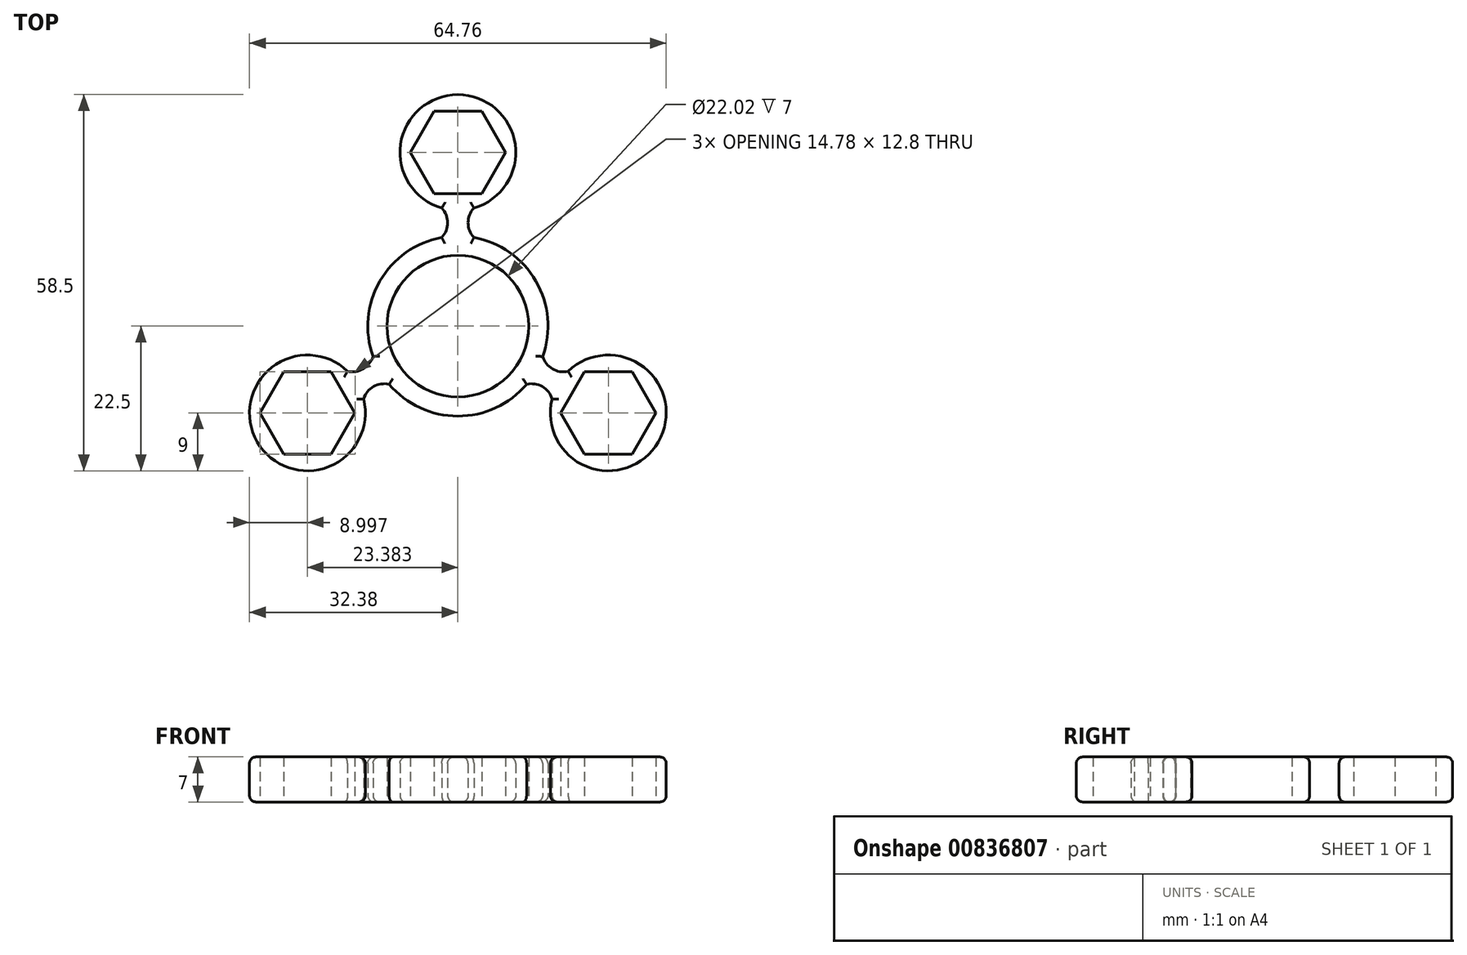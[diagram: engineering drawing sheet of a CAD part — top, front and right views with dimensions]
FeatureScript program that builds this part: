
annotation { "Feature Type Name" : "Feature", "Feature Type Description" : "" }
export const myFeature = defineFeature(function(context is Context, id is Id, definition is map)
    precondition{}
    {
        {
            var Q0;
            Q0=qCreatedBy(makeId("Top.planeOp"),FACE);
            var sketch = newSketch(context, id + "F0", { "sketchPlane" : qUnion([Q0])});
            skCircle(sketch, "E0", {"center": v(0, 0) * mm, "radius": 11.01 * mm});
            skArc(sketch, "E1", {"start": v(-2.5, 13.77) * mm, "mid": v(-12.12, 7) * mm, "end": v(-13.18, -4.72) * mm});
            skCircle(sketch, "E2.cCircle", {"center": v(0, 27) * mm, "radius": 6.4 * mm, "construction": true});
            skLineSegment(sketch, "E2.0", {"start": v(-7.4, 27) * mm, "end": v(-3.7, 33.4) * mm});
            skLineSegment(sketch, "E2.1", {"start": v(-3.7, 33.4) * mm, "end": v(3.7, 33.4) * mm});
            skLineSegment(sketch, "E2.2", {"start": v(3.7, 33.4) * mm, "end": v(7.4, 27) * mm});
            skLineSegment(sketch, "E2.3", {"start": v(7.4, 27) * mm, "end": v(3.7, 20.6) * mm});
            skLineSegment(sketch, "E2.4", {"start": v(3.7, 20.6) * mm, "end": v(-3.7, 20.6) * mm});
            skLineSegment(sketch, "E2.5", {"start": v(-3.7, 20.6) * mm, "end": v(-7.4, 27) * mm});
            skPoint(sketch, "E2.0.midPoint", {"position": v(-5.54, 30.2) * mm});
            skArc(sketch, "E3", {"start": v(2.5, 18.35) * mm, "mid": v(0, 36) * mm, "end": v(-2.5, 18.35) * mm});
            skArc(sketch, "E4", {"start": v(-2.5, 13.77) * mm, "mid": v(-1.59, 16.06) * mm, "end": v(-2.5, 18.35) * mm});
            skArc(sketch, "E5.MirrorCS", {"start": v(2.5, 13.77) * mm, "mid": v(1.59, 16.06) * mm, "end": v(2.5, 18.35) * mm});
            skArc(sketch, "E6.1.0", {"start": v(-17.15, -7.01) * mm, "mid": v(-31.18, -18) * mm, "end": v(-14.65, -11.34) * mm});
            skLineSegment(sketch, "E6.1.1", {"start": v(-27.08, -19.9) * mm, "end": v(-30.77, -13.5) * mm});
            skLineSegment(sketch, "E6.1.2", {"start": v(-19.69, -19.9) * mm, "end": v(-27.08, -19.9) * mm});
            skLineSegment(sketch, "E6.1.3", {"start": v(-16, -13.5) * mm, "end": v(-19.69, -19.9) * mm});
            skLineSegment(sketch, "E6.1.4", {"start": v(-19.69, -7.1) * mm, "end": v(-16, -13.5) * mm});
            skLineSegment(sketch, "E6.1.5", {"start": v(-27.08, -7.1) * mm, "end": v(-19.69, -7.1) * mm});
            skLineSegment(sketch, "E6.1.6", {"start": v(-30.77, -13.5) * mm, "end": v(-27.08, -7.1) * mm});
            skArc(sketch, "E6.1.7", {"start": v(-13.18, -4.72) * mm, "mid": v(-14.7, -6.66) * mm, "end": v(-17.15, -7.01) * mm});
            skArc(sketch, "E6.1.8", {"start": v(-10.68, -9.05) * mm, "mid": v(-13.12, -9.4) * mm, "end": v(-14.65, -11.34) * mm});
            skArc(sketch, "E6.2.0", {"start": v(14.65, -11.34) * mm, "mid": v(31.18, -18) * mm, "end": v(17.15, -7.01) * mm});
            skLineSegment(sketch, "E6.2.1", {"start": v(30.77, -13.5) * mm, "end": v(27.08, -19.9) * mm});
            skLineSegment(sketch, "E6.2.2", {"start": v(27.08, -7.1) * mm, "end": v(30.77, -13.5) * mm});
            skLineSegment(sketch, "E6.2.3", {"start": v(19.69, -7.1) * mm, "end": v(27.08, -7.1) * mm});
            skLineSegment(sketch, "E6.2.4", {"start": v(16, -13.5) * mm, "end": v(19.69, -7.1) * mm});
            skLineSegment(sketch, "E6.2.5", {"start": v(19.69, -19.9) * mm, "end": v(16, -13.5) * mm});
            skLineSegment(sketch, "E6.2.6", {"start": v(27.08, -19.9) * mm, "end": v(19.69, -19.9) * mm});
            skArc(sketch, "E6.2.7", {"start": v(10.68, -9.05) * mm, "mid": v(13.12, -9.4) * mm, "end": v(14.65, -11.34) * mm});
            skArc(sketch, "E6.2.8", {"start": v(13.18, -4.72) * mm, "mid": v(14.7, -6.66) * mm, "end": v(17.15, -7.01) * mm});
            skArc(sketch, "E7.trimOffspring", {"start": v(-10.68, -9.05) * mm, "mid": v(0, -14) * mm, "end": v(10.68, -9.05) * mm});
            skArc(sketch, "E8.trimOffspring", {"start": v(13.18, -4.72) * mm, "mid": v(12.12, 7) * mm, "end": v(2.5, 13.77) * mm});
            skSolve(sketch);
        }
        {
            var Q0;
            Q0 = qSketchRegion(id + "F0", true);
            extrude(context, id + "F1", {"entities" : qUnion([Q0]), "depth" : 7 * mm, "offsetDistance" : 25 * mm});
        }
        {
            var Q0;
            Q0=makeQuery(id+"F1.opExtrude","CAP_EDGE",EDGE,{"disambiguationData":[OSD([sQuery(id+"F0.wireOp",EDGE,"E4")])],"isStart":false});
            var Q1;
            Q1=makeQuery(id+"F1.opExtrude","CAP_EDGE",EDGE,{"disambiguationData":[OSD([sQuery(id+"F0.wireOp",EDGE,"E3")])],"isStart":false});
            var Q2;
            Q2=makeQuery(id+"F1.opExtrude","CAP_EDGE",EDGE,{"disambiguationData":[OSD([sQuery(id+"F0.wireOp",EDGE,"E5.MirrorCS")])],"isStart":false});
            var Q3;
            Q3=makeQuery(id+"F1.opExtrude","CAP_EDGE",EDGE,{"disambiguationData":[OSD([sQuery(id+"F0.wireOp",EDGE,"E8.trimOffspring")])],"isStart":false});
            var Q4;
            Q4=makeQuery(id+"F1.opExtrude","CAP_EDGE",EDGE,{"disambiguationData":[OSD([sQuery(id+"F0.wireOp",EDGE,"E6.2.8")])],"isStart":false});
            var Q5;
            Q5=makeQuery(id+"F1.opExtrude","CAP_EDGE",EDGE,{"disambiguationData":[OSD([sQuery(id+"F0.wireOp",EDGE,"E6.2.0")])],"isStart":false});
            var Q6;
            Q6=makeQuery(id+"F1.opExtrude","CAP_EDGE",EDGE,{"disambiguationData":[OSD([sQuery(id+"F0.wireOp",EDGE,"E6.2.7")])],"isStart":false});
            var Q7;
            Q7=makeQuery(id+"F1.opExtrude","CAP_EDGE",EDGE,{"disambiguationData":[OSD([sQuery(id+"F0.wireOp",EDGE,"E7.trimOffspring")])],"isStart":false});
            var Q8;
            Q8=makeQuery(id+"F1.opExtrude","CAP_EDGE",EDGE,{"disambiguationData":[OSD([sQuery(id+"F0.wireOp",EDGE,"E6.1.8")])],"isStart":false});
            var Q9;
            Q9=makeQuery(id+"F1.opExtrude","CAP_EDGE",EDGE,{"disambiguationData":[OSD([sQuery(id+"F0.wireOp",EDGE,"E6.1.7")])],"isStart":false});
            var Q10;
            Q10=makeQuery(id+"F1.opExtrude","CAP_EDGE",EDGE,{"disambiguationData":[OSD([sQuery(id+"F0.wireOp",EDGE,"E6.1.0")])],"isStart":false});
            var Q11;
            Q11=makeQuery(id+"F1.opExtrude","CAP_EDGE",EDGE,{"disambiguationData":[OSD([sQuery(id+"F0.wireOp",EDGE,"E1")])],"isStart":false});
            var Q12;
            Q12=makeQuery(id+"F1.opExtrude","CAP_EDGE",EDGE,{"disambiguationData":[OSD([sQuery(id+"F0.wireOp",EDGE,"E3")])],"isStart":true});
            var Q13;
            Q13=makeQuery(id+"F1.opExtrude","CAP_EDGE",EDGE,{"disambiguationData":[OSD([sQuery(id+"F0.wireOp",EDGE,"E4")])],"isStart":true});
            var Q14;
            Q14=makeQuery(id+"F1.opExtrude","CAP_EDGE",EDGE,{"disambiguationData":[OSD([sQuery(id+"F0.wireOp",EDGE,"E5.MirrorCS")])],"isStart":true});
            var Q15;
            Q15=makeQuery(id+"F1.opExtrude","CAP_EDGE",EDGE,{"disambiguationData":[OSD([sQuery(id+"F0.wireOp",EDGE,"E8.trimOffspring")])],"isStart":true});
            var Q16;
            Q16=makeQuery(id+"F1.opExtrude","CAP_EDGE",EDGE,{"disambiguationData":[OSD([sQuery(id+"F0.wireOp",EDGE,"E6.2.8")])],"isStart":true});
            var Q17;
            Q17=makeQuery(id+"F1.opExtrude","CAP_EDGE",EDGE,{"disambiguationData":[OSD([sQuery(id+"F0.wireOp",EDGE,"E6.2.0")])],"isStart":true});
            var Q18;
            Q18=makeQuery(id+"F1.opExtrude","CAP_EDGE",EDGE,{"disambiguationData":[OSD([sQuery(id+"F0.wireOp",EDGE,"E6.2.7")])],"isStart":true});
            var Q19;
            Q19=makeQuery(id+"F1.opExtrude","CAP_EDGE",EDGE,{"disambiguationData":[OSD([sQuery(id+"F0.wireOp",EDGE,"E7.trimOffspring")])],"isStart":true});
            var Q20;
            Q20=makeQuery(id+"F1.opExtrude","CAP_EDGE",EDGE,{"disambiguationData":[OSD([sQuery(id+"F0.wireOp",EDGE,"E6.1.8")])],"isStart":true});
            var Q21;
            Q21=makeQuery(id+"F1.opExtrude","CAP_EDGE",EDGE,{"disambiguationData":[OSD([sQuery(id+"F0.wireOp",EDGE,"E6.1.0")])],"isStart":true});
            var Q22;
            Q22=makeQuery(id+"F1.opExtrude","CAP_EDGE",EDGE,{"disambiguationData":[OSD([sQuery(id+"F0.wireOp",EDGE,"E6.1.7")])],"isStart":true});
            var Q23;
            Q23=makeQuery(id+"F1.opExtrude","CAP_EDGE",EDGE,{"disambiguationData":[OSD([sQuery(id+"F0.wireOp",EDGE,"E1")])],"isStart":true});
            fillet(context, id + "F2", {"entities" : qUnion([Q0, Q1, Q2, Q3, Q4, Q5, Q6, Q7, Q8, Q9, Q10, Q11, Q12, Q13, Q14, Q15, Q16, Q17, Q18, Q19, Q20, Q21, Q22, Q23]), "radius" : 1 * mm, "tangentPropagation" : true, "allowEdgeOverflow" : false});
        }
    });
